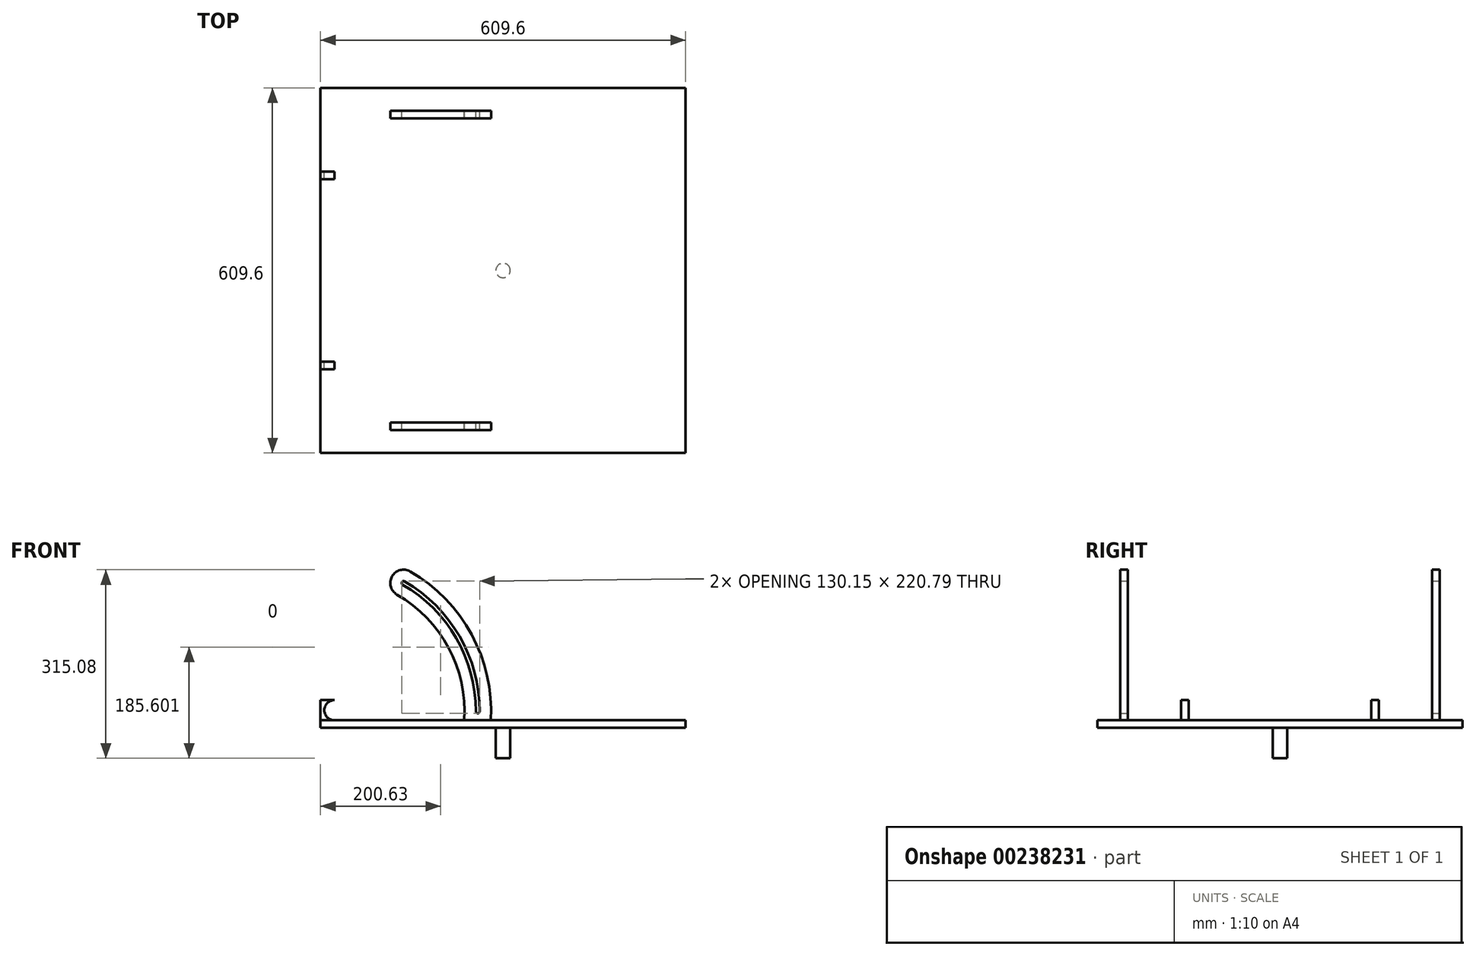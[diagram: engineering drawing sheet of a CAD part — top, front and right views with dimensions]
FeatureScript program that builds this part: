
annotation { "Feature Type Name" : "Feature", "Feature Type Description" : "" }
export const myFeature = defineFeature(function(context is Context, id is Id, definition is map)
    precondition{}
    {
        {
            var Q0;
            Q0=qCreatedBy(makeId("Top.planeOp"),FACE);
            var sketch = newSketch(context, id + "F0", { "sketchPlane" : qUnion([Q0])});
            skLineSegment(sketch, "E0.bottom", {"start": v(0, 0) * mm, "end": v(609.6, 0) * mm});
            skLineSegment(sketch, "E0.top", {"start": v(0, 609.6) * mm, "end": v(609.6, 609.6) * mm});
            skLineSegment(sketch, "E0.left", {"start": v(0, 0) * mm, "end": v(0, 609.6) * mm});
            skLineSegment(sketch, "E0.right", {"start": v(609.6, 0) * mm, "end": v(609.6, 609.6) * mm});
            skSolve(sketch);
        }
        {
            var Q0;
            Q0=makeQuery(id+"F0.imprint","IMPRINT",FACE,{"disambiguationData":[TD([[makeQuery(id+"F0.imprint","IMPRINT",EDGE,{"derivedFrom":sQuery(id+"F0.wireOp",EDGE,"E0.bottom")}),1.0]])]});
            extrude(context, id + "F1", {"entities" : qUnion([Q0]), "depth" : 12.7 * mm});
        }
        {
            var Q0;
            Q0=makeQuery(id+"F1.opExtrude","CAP_FACE",FACE,{"disambiguationData":[OSD([sQuery(id+"F0.wireOp",EDGE,"E0.bottom"),sQuery(id+"F0.wireOp",EDGE,"E0.top"),sQuery(id+"F0.wireOp",EDGE,"E0.left"),sQuery(id+"F0.wireOp",EDGE,"E0.right")])],"isStart":true});
            var sketch = newSketch(context, id + "F2", { "sketchPlane" : qUnion([Q0])});
            skPoint(sketch, "E1.orphan", {"position": v(304.8, -609.6) * mm});
            skPoint(sketch, "E2.orphan", {"position": v(609.6, -304.8) * mm});
            skPoint(sketch, "E3", {"position": v(304.8, -304.8) * mm});
            skCircle(sketch, "E4", {"center": v(304.8, -304.8) * mm, "radius": 12.06 * mm});
            skSolve(sketch);
        }
        {
            var Q0;
            Q0=makeQuery(id+"F2.imprint","IMPRINT",FACE,{"disambiguationData":[TD([[makeQuery(id+"F2.imprint","IMPRINT",EDGE,{"derivedFrom":sQuery(id+"F2.wireOp",EDGE,"E4")}),1.0]])]});
            extrude(context, id + "F3", {"entities" : qUnion([Q0]), "operationType" : NewBodyOperationType.ADD, "depth" : 50.8 * mm});
        }
        {
            var Q0;
            Q0=qCreatedBy(makeId("Front.planeOp"),FACE);
            cPlane(context, id + "F4", {"entities" : qUnion([Q0]), "cplaneType" : CPlaneType.OFFSET, "offset" : 304.8 * mm, "oppositeDirection" : true, "width" : 152.4 * mm, "height" : 152.4 * mm});
        }
        {
            var Q0;
            Q0=qCreatedBy(id+"F4.planeOp",FACE);
            var sketch = newSketch(context, id + "F5", { "sketchPlane" : qUnion([Q0])});
            skPoint(sketch, "E5.0", {"position": v(0, 12.7) * mm});
            skLineSegment(sketch, "E6", {"start": v(0, 12.7) * mm, "end": v(0, 46.36) * mm});
            skPoint(sketch, "E7.endSnap0", {"position": v(16.83, 46.36) * mm});
            skLineSegment(sketch, "E8", {"start": v(0, 29.53) * mm, "end": v(16.83, 29.53) * mm, "construction": true});
            skPoint(sketch, "E9.orphan", {"position": v(16.83, 38.6) * mm});
            skPoint(sketch, "E10.orphan", {"position": v(33.66, 12.7) * mm});
            skLineSegment(sketch, "E11", {"start": v(16.83, 29.53) * mm, "end": v(23.18, 29.53) * mm, "construction": true});
            skCircle(sketch, "E12", {"center": v(23.18, 29.53) * mm, "radius": 16.83 * mm});
            skLineSegment(sketch, "E13", {"start": v(0, 12.7) * mm, "end": v(23.18, 12.7) * mm});
            skLineSegment(sketch, "E14", {"start": v(0, 46.36) * mm, "end": v(23.18, 46.36) * mm});
            skSolve(sketch);
        }
        {
            var Q0;
            Q0=qCreatedBy(id+"F4.planeOp",FACE);
            var sketch = newSketch(context, id + "F6", { "sketchPlane" : qUnion([Q0])});
            skPoint(sketch, "E15.0", {"position": v(14.88, 27.58) * mm});
            skArc(sketch, "E16", {"start": v(262.08, 12.7) * mm, "mid": v(262.42, 20.14) * mm, "end": v(262.53, 27.58) * mm, "construction": true});
            skArc(sketch, "E17", {"start": v(259.35, 27.58) * mm, "mid": v(226.6, 149.82) * mm, "end": v(137.12, 239.3) * mm});
            skArc(sketch, "E18", {"start": v(265.7, 27.58) * mm, "mid": v(232.1, 153) * mm, "end": v(140.3, 244.8) * mm});
            skArc(sketch, "E19", {"start": v(239.81, 12.7) * mm, "mid": v(213.72, 133.78) * mm, "end": v(127.6, 222.8) * mm});
            skArc(sketch, "E20", {"start": v(284.34, 12.7) * mm, "mid": v(252.23, 156.02) * mm, "end": v(149.82, 261.3) * mm});
            skLineSegment(sketch, "E21", {"start": v(14.88, 27.58) * mm, "end": v(259.35, 27.58) * mm, "construction": true});
            skLineSegment(sketch, "E22", {"start": v(14.88, 27.58) * mm, "end": v(170.79, 297.62) * mm, "construction": true});
            skPoint(sketch, "E23.0", {"position": v(0, 12.7) * mm});
            skLineSegment(sketch, "E24", {"start": v(0, 12.7) * mm, "end": v(662.26, 12.7) * mm});
            skArc(sketch, "E25", {"start": v(149.82, 261.3) * mm, "mid": v(119.46, 253.16) * mm, "end": v(127.6, 222.8) * mm});
            skArc(sketch, "E26", {"start": v(140.3, 244.8) * mm, "mid": v(135.95, 243.64) * mm, "end": v(137.12, 239.3) * mm});
            skArc(sketch, "E27", {"start": v(259.35, 27.58) * mm, "mid": v(262.53, 24.4) * mm, "end": v(265.7, 27.58) * mm});
            skArc(sketch, "E28.trimOffspring", {"start": v(262.5, 30.75) * mm, "mid": v(228.55, 152.78) * mm, "end": v(138.7, 242.05) * mm, "construction": true});
            skLineSegment(sketch, "E29", {"start": v(239.81, 12.7) * mm, "end": v(284.34, 12.7) * mm});
            skSolve(sketch);
        }
        {
            var Q0;
            {var subQ9=sQuery(id+"F6.wireOp",EDGE,"E19");Q0=makeQuery(id+"F6.imprint","IMPRINT",FACE,{"disambiguationData":[TD([[makeQuery(id+"F6.imprint","IMPRINT",EDGE,{"derivedFrom":subQ9}),-1.0]])]});}
            extrude(context, id + "F7", {"entities" : qUnion([Q0]), "operationType" : NewBodyOperationType.ADD, "endBound" : BoundingType.SYMMETRIC, "depth" : 533.4 * mm});
        }
        {
            var Q0;
            Q0 = qSketchRegion(id + "F6", true);
            extrude(context, id + "F8", {"entities" : qUnion([Q0]), "operationType" : NewBodyOperationType.REMOVE, "endBound" : BoundingType.SYMMETRIC, "oppositeDirection" : true, "depth" : 508 * mm});
        }
        {
            var Q0;
            Q0=makeQuery(id+"F5.imprint","IMPRINT",FACE,{"disambiguationData":[TD([[makeQuery(id+"F5.imprint","IMPRINT",EDGE,{"derivedFrom":sQuery(id+"F5.wireOp",EDGE,"E6")}),-1.0]])]});
            extrude(context, id + "F9", {"entities" : qUnion([Q0]), "operationType" : NewBodyOperationType.ADD, "endBound" : BoundingType.SYMMETRIC, "depth" : 330.2 * mm});
        }
        {
            var Q0;
            Q0=makeQuery(id+"F5.imprint","IMPRINT",FACE,{"disambiguationData":[TD([[makeQuery(id+"F5.imprint","IMPRINT",EDGE,{"derivedFrom":sQuery(id+"F5.wireOp",EDGE,"E6")}),-1.0]])]});
            extrude(context, id + "F10", {"entities" : qUnion([Q0]), "operationType" : NewBodyOperationType.REMOVE, "endBound" : BoundingType.SYMMETRIC, "oppositeDirection" : true, "depth" : 304.8 * mm});
        }
    });
